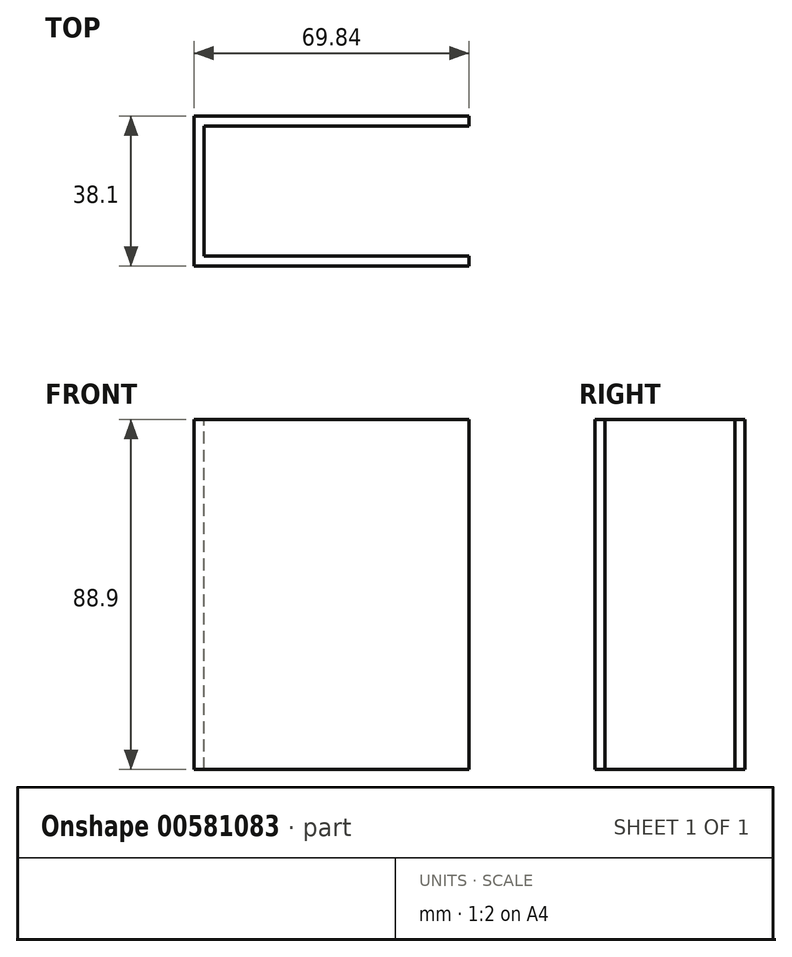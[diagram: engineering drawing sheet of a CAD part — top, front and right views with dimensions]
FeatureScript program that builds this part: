
annotation { "Feature Type Name" : "Feature", "Feature Type Description" : "" }
export const myFeature = defineFeature(function(context is Context, id is Id, definition is map)
    precondition{}
    {
        {
            var Q0;
            Q0=qCreatedBy(makeId("Front.planeOp"),FACE);
            var sketch = newSketch(context, id + "F0", { "sketchPlane" : qUnion([Q0])});
            skLineSegment(sketch, "E0", {"start": v(0, 76.63) * mm, "end": v(0, -86.5) * mm, "construction": true});
            skLineSegment(sketch, "E1", {"start": v(-79.84, 0) * mm, "end": v(91.2, 0) * mm, "construction": true});
            skLineSegment(sketch, "E2", {"start": v(-34.92, 44.45) * mm, "end": v(34.92, 44.45) * mm});
            skLineSegment(sketch, "E3", {"start": v(34.93, 44.45) * mm, "end": v(34.92, -44.45) * mm});
            skLineSegment(sketch, "E4", {"start": v(34.93, -44.45) * mm, "end": v(-34.92, -44.45) * mm});
            skLineSegment(sketch, "E5", {"start": v(-34.92, -44.45) * mm, "end": v(-34.93, 44.45) * mm});
            skSolve(sketch);
        }
        {
            var Q0;
            Q0 = qSketchRegion(id + "F0", true);
            extrude(context, id + "F1", {"entities" : qUnion([Q0]), "oppositeDirection" : true, "depth" : 38.1 * mm, "offsetDistance" : 25.4 * mm});
        }
        {
            var Q0;
            Q0=makeQuery(id+"F1.opExtrude","SWEPT_FACE",FACE,{"disambiguationData":[OSD([sQuery(id+"F0.wireOp",EDGE,"E2")])]});
            var Q1;
            Q1=makeQuery(id+"F1.opExtrude","SWEPT_FACE",FACE,{"disambiguationData":[OSD([sQuery(id+"F0.wireOp",EDGE,"E3")])]});
            var Q2;
            Q2=makeQuery(id+"F1.opExtrude","SWEPT_FACE",FACE,{"disambiguationData":[OSD([sQuery(id+"F0.wireOp",EDGE,"E4")])]});
            shell(context, id + "F2", {"entities" : qUnion([Q0, Q1, Q2]), "thickness" : 2.54 * mm});
        }
    });
